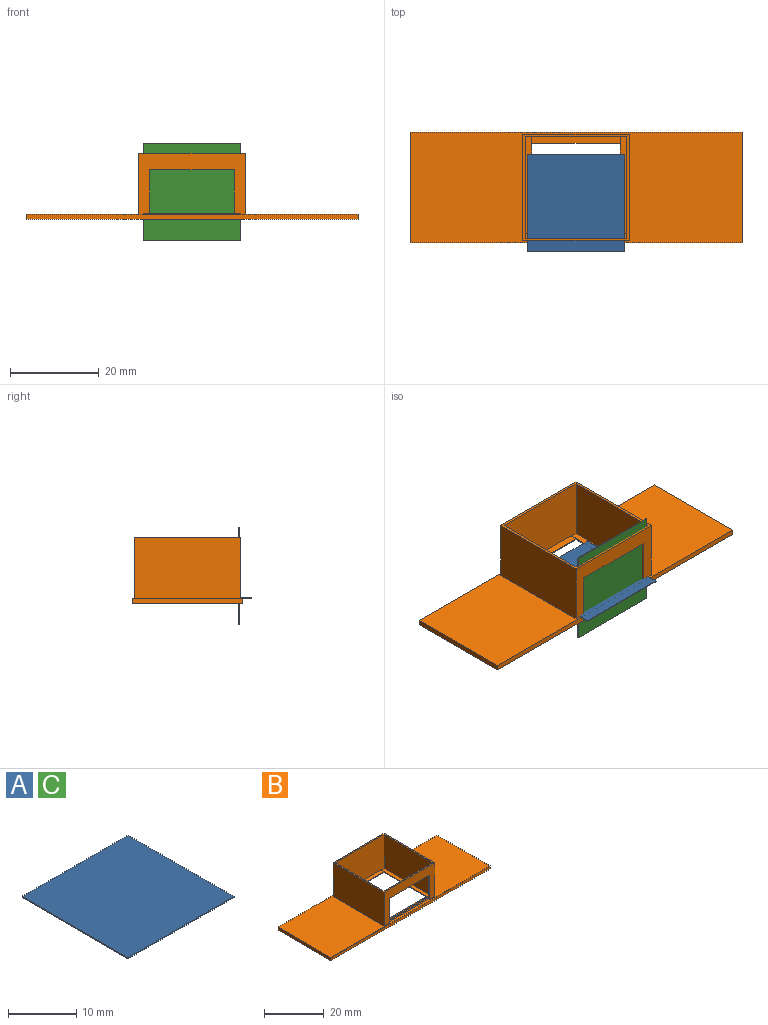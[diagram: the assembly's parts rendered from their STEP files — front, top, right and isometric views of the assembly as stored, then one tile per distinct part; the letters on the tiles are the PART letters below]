
ASSEMBLY  parts=3 mates=2
PART A: 6 faces, bbox 22x22x0.2 mm
  f0: plane 22x0.17mm, normal (0,-1,0), area 3.7mm2, adj f1,f3,f4,f5
  f1: plane 22x0.17mm, normal (1,0,0), area 3.7mm2, adj f0,f2,f4,f5
  f2: plane 22x0.17mm, normal (0,1,0), area 3.7mm2, adj f1,f3,f4,f5
  f3: plane 22x0.17mm, normal (-1,0,0), area 3.7mm2, adj f0,f2,f4,f5
  f4: plane 22x22mm, normal (0,0,1), area 484mm2, adj f0,f1,f2,f3
  f5: plane 22x22mm, normal (0,0,-1), area 484mm2, adj f0,f1,f2,f3
PART B: 34 faces, bbox 75x25x15 mm
  f0: plane 20x0.22mm, normal (-1,0,0), area 4.4mm2, adj f2,f4,f5,f8,f26,f33
  f1: plane 20x0.22mm, normal (1,0,0), area 4.4mm2, adj f2,f4,f5,f8,f27,f29
  f2: plane 20x0.2mm, normal (0,-1,0), area 4mm2, adj f0,f1,f5,f28
  f3: plane 23x13.78mm, normal (0,-1,0), area 313.3mm2, adj f4,f17,f19,f21,f30,f31,f32
  f4: plane 23x22mm, normal (0,0,1), area 75mm2, adj f0,f1,f3,f8,f17,f19,f23,f29
  f5: plane 75x25mm, normal (0,0,1), area 1349.7mm2, adj f0,f1,f2,f6,f7,f9,f10,f11
  f6: plane 10x0.5mm, normal (1,0,0), area 5mm2, adj f5,f14,f18,f22
  f7: plane 10x0.5mm, normal (-1,0,0), area 5mm2, adj f5,f14,f18,f22
  f8: plane 20x0.22mm, normal (0,1,0), area 4.4mm2, adj f0,f1,f4,f25
  f9: plane 75x1.2mm, normal (0,-1,0), area 90mm2, adj f5,f10,f12,f13
  f10: plane 25x1.2mm, normal (1,0,0), area 30mm2, adj f5,f9,f11,f13
  f11: plane 75x1.2mm, normal (0,1,0), area 90mm2, adj f5,f10,f12,f13
  f12: plane 25x1.2mm, normal (-1,0,0), area 30mm2, adj f5,f9,f11,f13
  f13: plane 75x25mm, normal (0,0,-1), area 1324.4mm2, adj f9,f10,f11,f12,f25,f26,f27,f28
  f14: plane 24x13.8mm, normal (0,-1,0), area 141.2mm2, adj f5,f6,f7,f15,f20,f21,f22
  f15: plane 24x13.8mm, normal (1,0,0), area 331.2mm2, adj f5,f14,f16,f21
  f16: plane 24x13.8mm, normal (0,1,0), area 327.1mm2, adj f5,f15,f20,f21,f30,f31,f32
  f17: plane 23x14.28mm, normal (-1,0,0), area 317.4mm2, adj f3,f4,f18,f21,f23,f24
  f18: plane 23x14.28mm, normal (0,1,0), area 138.4mm2, adj f5,f6,f7,f17,f19,f21,f22,f24
  f19: plane 23x14.28mm, normal (1,0,0), area 317.4mm2, adj f3,f4,f18,f21,f23,f24
  f20: plane 24x13.8mm, normal (-1,0,0), area 331.2mm2, adj f5,f14,f16,f21
  f21: plane 24x24mm, normal (0,0,1), area 47mm2, adj f3,f14,f15,f16,f17,f18,f19,f20
  f22: plane 19.01x0.5mm, normal (0,0,-1), area 9.5mm2, adj f6,f7,f14,f18
  f23: plane 23x0.5mm, normal (0,-1,0), area 11.5mm2, adj f4,f17,f19,f24
  f24: plane 23x1mm, normal (0,0,1), area 23mm2, adj f17,f18,f19,f23
  f25: plane 23.46x1.73mm, normal (0,0.5,-0.87), area 43.5mm2, adj f8,f13,f26,f27
  f26: plane 23.46x1.73mm, normal (-0.5,0,-0.87), area 43.5mm2, adj f0,f13,f25,f28
  f27: plane 23.46x1.73mm, normal (0.5,0,-0.87), area 43.5mm2, adj f1,f13,f25,f28
  f28: plane 23.46x1.73mm, normal (0,-0.5,-0.87), area 43.5mm2, adj f2,f13,f26,f27
  f29: plane 0.15x0.02mm, normal (0,1,0), area 0mm2, adj f1,f4,f5,f32
  f30: plane 20.3x0.5mm, normal (0,0,-1), area 10.2mm2, adj f3,f16,f31,f32
  f31: plane 4x0.2mm, normal (-1,0,0), area 0.2mm2, adj f3,f4,f5,f16,f30,f33
  f32: plane 4x0.2mm, normal (1,0,0), area 0.2mm2, adj f3,f4,f5,f16,f29,f30
  f33: plane 0.15x0.02mm, normal (0,1,0), area 0mm2, adj f0,f4,f5,f31
PART C: same geometry as A
PLACE A t=(-32.64,-25.72,-5.14)mm
PLACE B t=(-32.64,-22.16,-6.36)mm
PLACE C rot(axis=(1,0,0),90deg) t=(-32.64,-33.66,-0.16)mm
MATE parallel C.f5 <-> B.f18  axis (0,1,0) through (-32.64,-33.66,-0.16)mm
MATE slider A.f5 <-> B.f4  axis (0,0,-1) through (-32.64,-25.72,-5.14)mm
